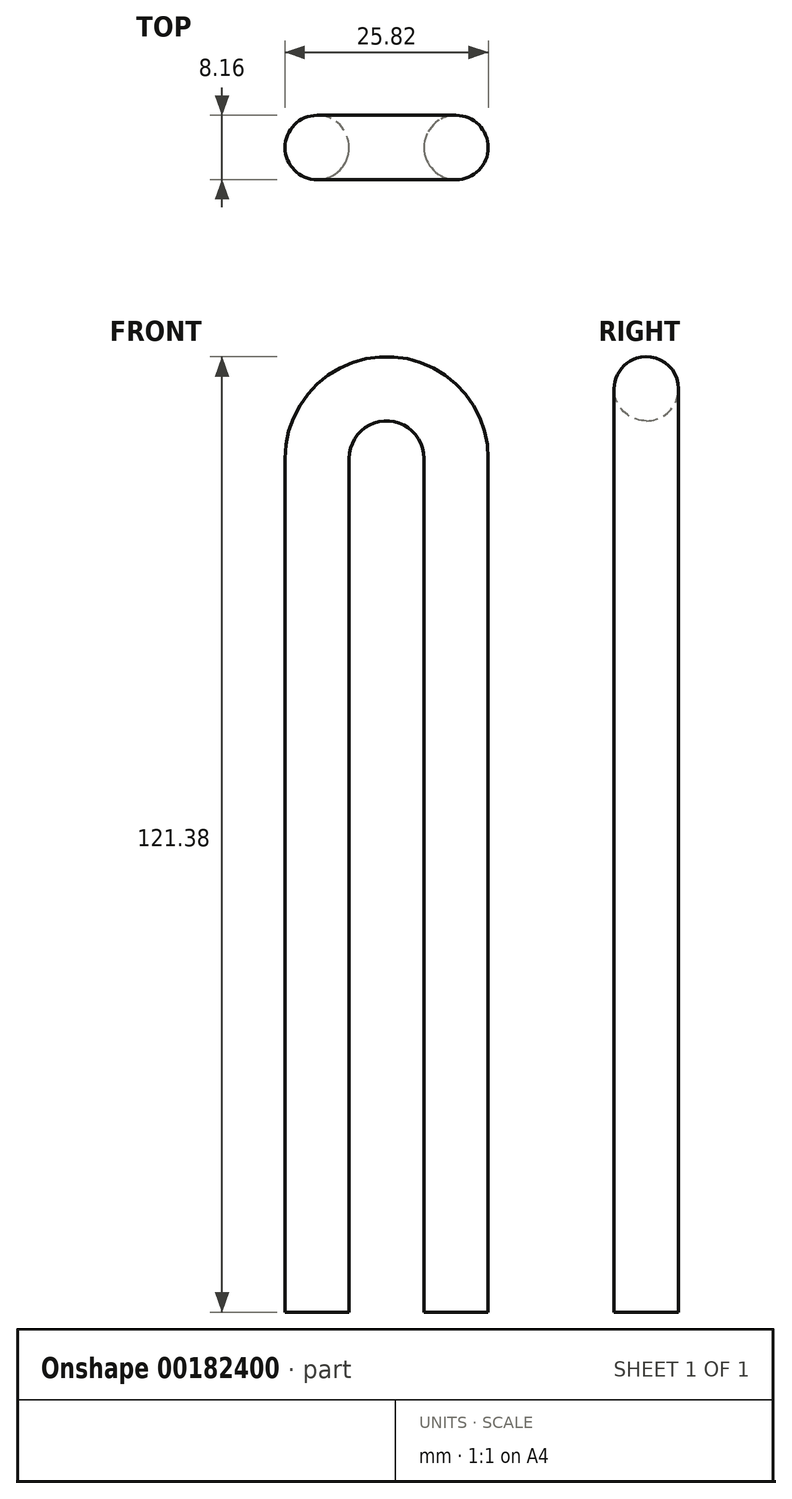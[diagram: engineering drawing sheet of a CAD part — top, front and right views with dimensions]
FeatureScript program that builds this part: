
annotation { "Feature Type Name" : "Feature", "Feature Type Description" : "" }
export const myFeature = defineFeature(function(context is Context, id is Id, definition is map)
    precondition{}
    {
        {
            var Q0;
            Q0=qCreatedBy(makeId("Front.planeOp"),FACE);
            var sketch = newSketch(context, id + "F0", { "sketchPlane" : qUnion([Q0])});
            skLineSegment(sketch, "E0", {"start": v(-63.17, -46.04) * mm, "end": v(-63.17, 62.43) * mm});
            skArc(sketch, "E1", {"start": v(-63.17, 62.43) * mm, "mid": v(-54.34, 71.26) * mm, "end": v(-45.51, 62.43) * mm});
            skLineSegment(sketch, "E2", {"start": v(-45.51, 62.43) * mm, "end": v(-45.51, -46.04) * mm});
            skSolve(sketch);
        }
        {
            var Q0;
            Q0=qCreatedBy(makeId("Top.planeOp"),FACE);
            var sketch = newSketch(context, id + "F1", { "sketchPlane" : qUnion([Q0])});
            skCircle(sketch, "E3", {"center": v(-63.17, 0) * mm, "radius": 4.08 * mm});
            skSolve(sketch);
        }
        {
            var Q0;
            Q0=makeQuery(id+"F1.imprint","IMPRINT",FACE,{"disambiguationData":[TD([[makeQuery(id+"F1.imprint","IMPRINT",EDGE,{"derivedFrom":sQuery(id+"F1.wireOp",EDGE,"E3")}),1.0]])]});
            var Q1;
            Q1 = qConstructionFilter(qBodyType(qCreatedBy(id + "F0" ,EDGE), BodyType.WIRE), ConstructionObject.NO);
            sweep(context, id + "F2", {"profiles" : qUnion([Q0]), "path" : qUnion([Q1])});
        }
    });
